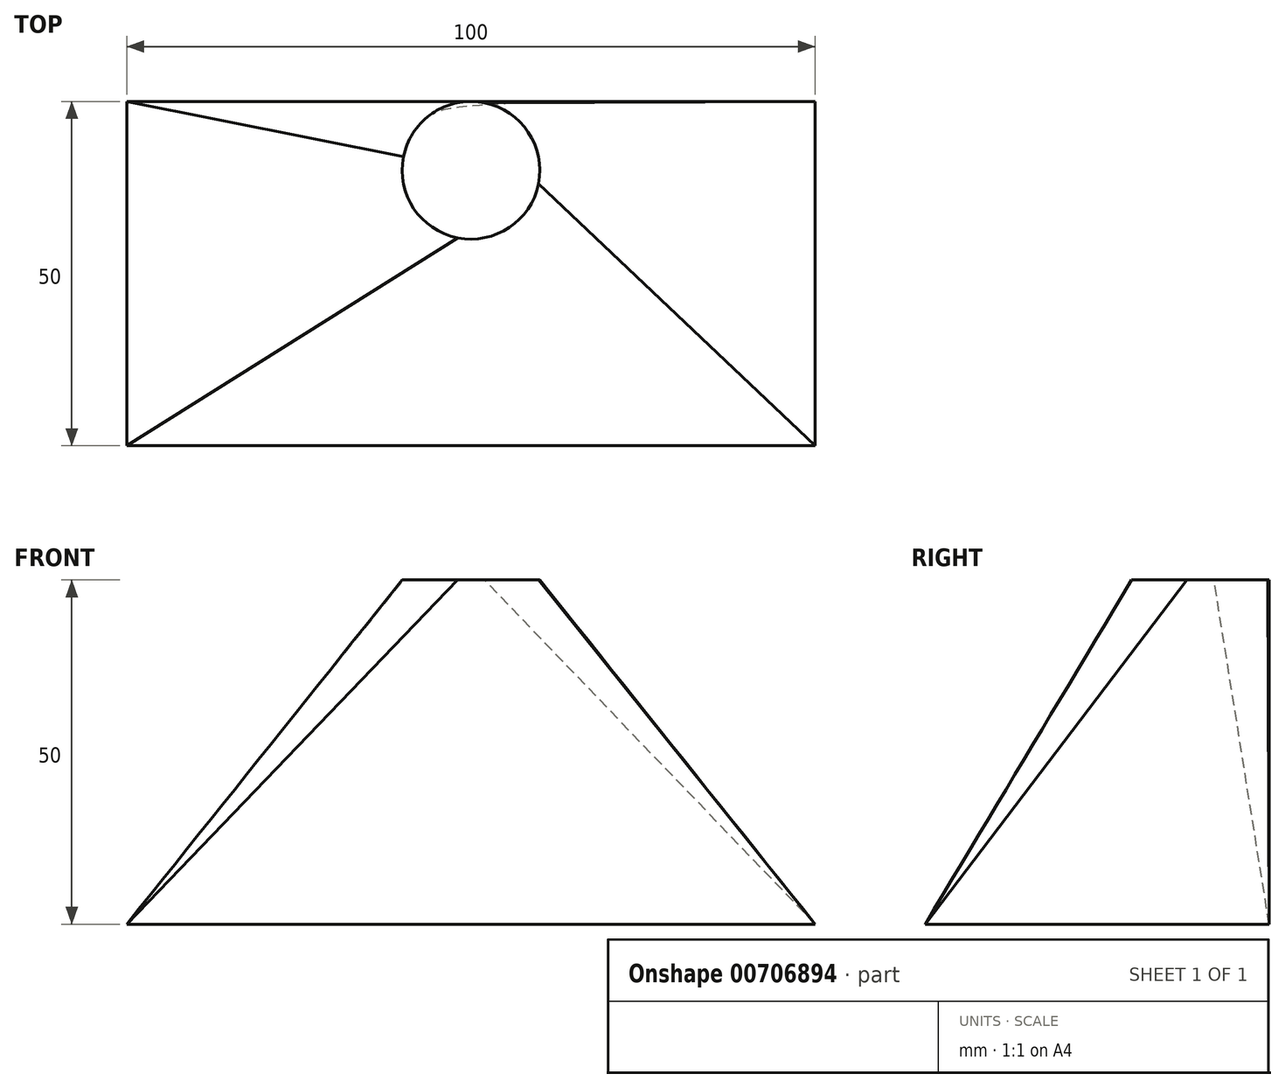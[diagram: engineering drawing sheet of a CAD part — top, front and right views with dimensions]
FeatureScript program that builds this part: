
annotation { "Feature Type Name" : "Feature", "Feature Type Description" : "" }
export const myFeature = defineFeature(function(context is Context, id is Id, definition is map)
    precondition{}
    {
        {
            var Q0;
            Q0=qCreatedBy(makeId("Top.planeOp"),FACE);
            var sketch = newSketch(context, id + "F0", { "sketchPlane" : qUnion([Q0])});
            skLineSegment(sketch, "E0.bottom", {"start": v(-50, 0) * mm, "end": v(50, 0) * mm});
            skLineSegment(sketch, "E0.top", {"start": v(-50, -50) * mm, "end": v(50, -50) * mm});
            skLineSegment(sketch, "E0.left", {"start": v(-50, 0) * mm, "end": v(-50, -50) * mm});
            skLineSegment(sketch, "E0.right", {"start": v(50, 0) * mm, "end": v(50, -50) * mm});
            skSolve(sketch);
        }
        {
            var Q0;
            Q0=qCreatedBy(makeId("Top.planeOp"),FACE);
            cPlane(context, id + "F1", {"entities" : qUnion([Q0]), "cplaneType" : CPlaneType.OFFSET, "offset" : 50 * mm, "width" : 150 * mm, "height" : 150 * mm});
        }
        {
            var Q0;
            Q0=qCreatedBy(id+"F1.planeOp",FACE);
            var sketch = newSketch(context, id + "F2", { "sketchPlane" : qUnion([Q0])});
            skCircle(sketch, "E1", {"center": v(0, -10) * mm, "radius": 10 * mm});
            skSolve(sketch);
        }
        {
            var Q0;
            Q0=makeQuery(id+"F0.imprint","IMPRINT",FACE,{"disambiguationData":[TD([[makeQuery(id+"F0.imprint","IMPRINT",EDGE,{"derivedFrom":sQuery(id+"F0.wireOp",EDGE,"E0.bottom")}),-1.0]])]});
            var Q1;
            Q1=makeQuery(id+"F2.imprint","IMPRINT",FACE,{"disambiguationData":[TD([[makeQuery(id+"F2.imprint","IMPRINT",EDGE,{"derivedFrom":sQuery(id+"F2.wireOp",EDGE,"E1")}),1.0]])]});
            loft(context, id + "F3", {"sheetProfilesArray" : [{ "sheetProfileEntities" : qUnion([Q0]) }, { "sheetProfileEntities" : qUnion([Q1]) }]});
        }
    });
